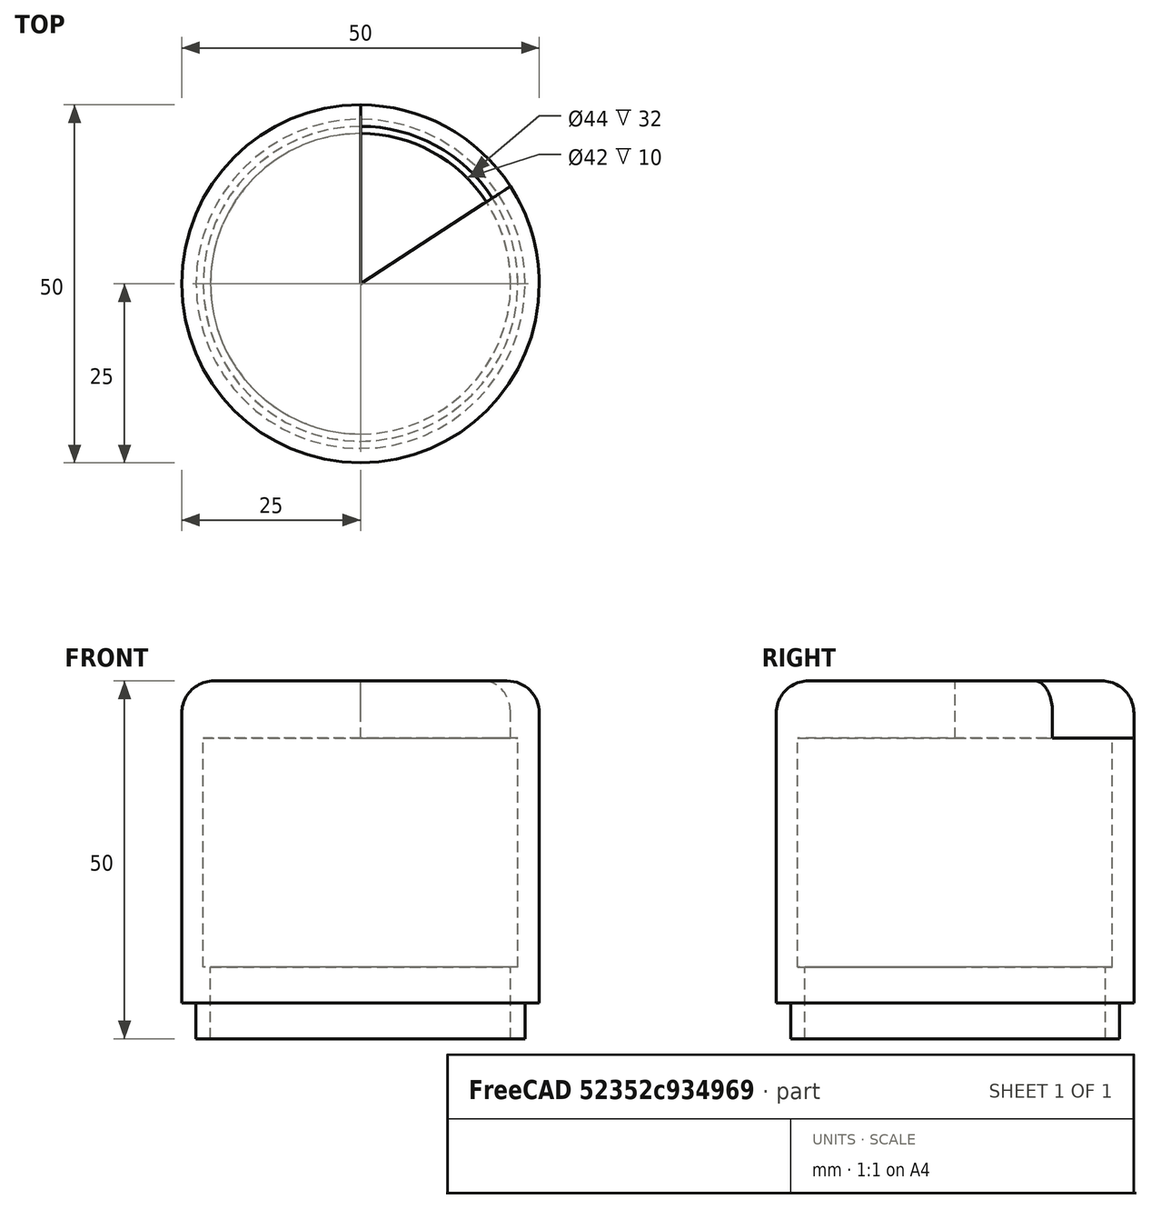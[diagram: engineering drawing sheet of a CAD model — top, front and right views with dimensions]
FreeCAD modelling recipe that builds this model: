
FCSTD DOCUMENT  (FreeCAD 0.14R3700 (Git))
Label: tapa v1.1 con agujero
License: CC-BY 3.0
LicenseURL: http://creativecommons.org/licenses/by/3.0/
objects: Part::Cylinder×5, Part::Cut×4, Part::Box×2, Part::Fillet×1, Part::MultiFuse×1
note: 13 computed .brp shape members not serialized (recipe doc carries the construction recipe); baked Part::Feature solids carry a one-line shape summary decoded from their .brp

FEATURE [Part::Cylinder] Cylinder  label="Cilindro"
  Angle = 360
  Height = 40
  Radius = 25
FEATURE [Part::Cylinder] Cylinder001  label="Cilindro001"
  Angle = 360
  Height = 37
  Radius = 22
FEATURE [Part::Cylinder] Cylinder002  label="Cilindro002"
  Angle = 360
  Height = 5
  Placement = pos=(0,0,40) rot=(0,0,1;0rad)
  Radius = 25
FEATURE [Part::Cylinder] Cylinder003  label="Cilindro003"
  Angle = 360
  Height = 10
  Radius = 23
FEATURE [Part::Cylinder] Cylinder004  label="Cilindro004"
  Angle = 360
  Height = 21
  Radius = 21
FEATURE [Part::Fillet] Fillet
  Base = -> Cylinder002
  Edges = 1 edges r=4.5: [Edge1]
FEATURE [Part::Cut] Cut
  Base = -> Cylinder
  Tool = -> Cylinder001
FEATURE [Part::Cut] Cut001
  Base = -> Cylinder003
  Placement = pos=(0,0,-5) rot=(0,0,1;0rad)
  Tool = -> Cylinder004
FEATURE [Part::Box] Box  label="Cubo"
  Height = 10
  Length = 37
  Placement = pos=(0,0,37) rot=(0,0,1;0rad)
  Width = 39
FEATURE [Part::Box] Box001  label="Cubo001"
  Height = 10
  Length = 37
  Placement = pos=(0,0,37) rot=(0,0,-1;0.994838rad)
  Width = 39
FEATURE [Part::Cut] Cut002
  Base = -> Box
  Tool = -> Box001
FEATURE [Part::MultiFuse] Fusion
  Shapes = -> [Fillet,Cut,Cut001]
FEATURE [Part::Cut] Cut003
  Base = -> Fusion
  Tool = -> Cut002
